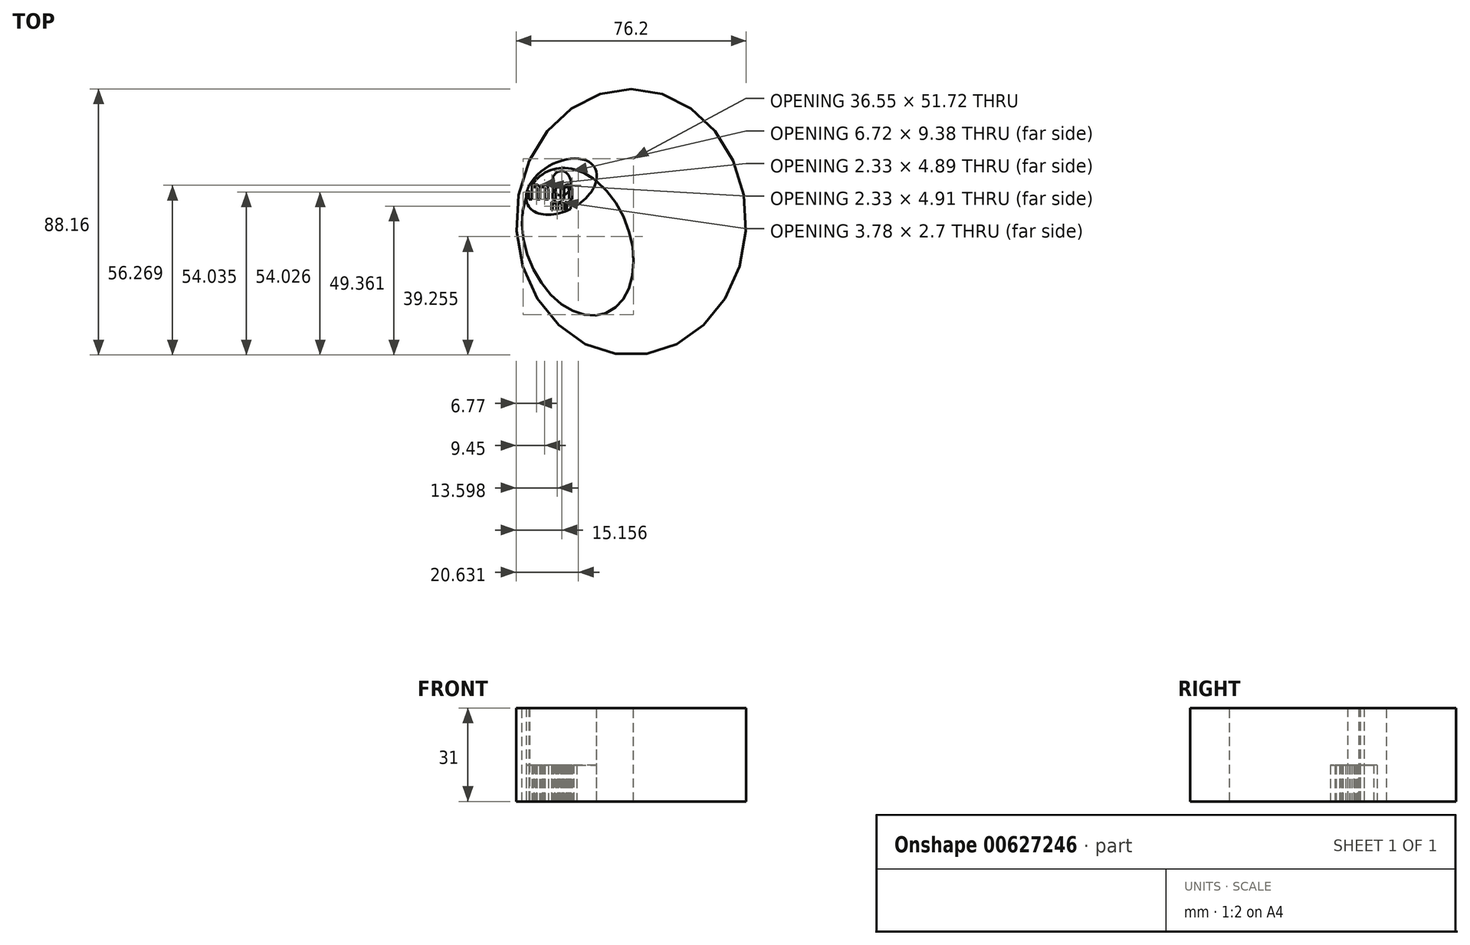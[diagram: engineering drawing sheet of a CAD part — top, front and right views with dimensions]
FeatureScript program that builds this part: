
annotation { "Feature Type Name" : "Feature", "Feature Type Description" : "" }
export const myFeature = defineFeature(function(context is Context, id is Id, definition is map)
    precondition{}
    {
        {
            var Q0;
            Q0=qCreatedBy(makeId("Top.planeOp"),FACE);
            var sketch = newSketch(context, id + "F0", { "sketchPlane" : qUnion([Q0])});
            skText(sketch, "E0", { "text": "mm", "fontName": "AllertaStencil-Regular.ttf"});
            skText(sketch, "E1", { "text": "mm", "fontName": "OpenSans-Regular.ttf"});
            skEllipse(sketch, "E2", {"center": v(-6.82, 3.93) * mm, "majorRadius": 6.35 * mm, "minorRadius": 2.55 * mm, "majorAxis": v(1, 0)});
            skEllipse(sketch, "E3", {"center": v(-5.46, 12.84) * mm, "majorRadius": 4.06 * mm, "minorRadius": 3.18 * mm, "majorAxis": v(0, -1)});
            skEllipse(sketch, "E4", {"center": v(-5.43, 11.73) * mm, "majorRadius": 7.98 * mm, "minorRadius": 12.7 * mm, "majorAxis": v(-0.49, 0.87)});
            skEllipse(sketch, "E5", {"center": v(17.67, 0) * mm, "majorRadius": 38.1 * mm, "minorRadius": 44.08 * mm, "majorAxis": v(1, 0)});
            skEllipse(sketch, "E6", {"center": v(0, -6.53) * mm, "majorRadius": 25.4 * mm, "minorRadius": 17.2 * mm, "majorAxis": v(-0.36, 0.93)});
            const initialGuessF0  = {"E0": [-0.01697, 0.0075, 1, 0, 0.00635], "E1": [-0.00915, 0.00393, 1, 0, 0.00357]};
            skSetInitialGuess(sketch, initialGuessF0);
            skSolve(sketch);
        }
        {
            var Q0;
            {var subQ16=sQuery(id+"F0.wireOp",EDGE,"E0.sketch_text.stroke-1");Q0=makeQuery(id+"F0.imprint","IMPRINT",FACE,{"disambiguationData":[TD([[makeQuery(id+"F0.imprint","IMPRINT",EDGE,{"derivedFrom":subQ16}),1.0]])]});}
            extrude(context, id + "F1", {"entities" : qUnion([Q0]), "depth" : 12 * mm, "offsetDistance" : 25.4 * mm});
        }
        {
            var Q0;
            Q0=makeQuery(id+"F0.imprint","IMPRINT",FACE,{"disambiguationData":[TD([[makeQuery(id+"F0.imprint","IMPRINT",EDGE,{"derivedFrom":sQuery(id+"F0.wireOp",EDGE,"E1.sketch_text.stroke-0")}),1.0]])]});
            extrude(context, id + "F2", {"entities" : qUnion([Q0]), "operationType" : NewBodyOperationType.ADD, "depth" : 12 * mm, "offsetDistance" : 25.4 * mm});
        }
        {
            var Q0;
            {var subQ2=sQuery(id+"F0.wireOp",EDGE,"E0.sketch_text.stroke-39");Q0=makeQuery(id+"F0.imprint","IMPRINT",FACE,{"disambiguationData":[TD([[makeQuery(id+"F0.imprint","IMPRINT",EDGE,{"derivedFrom":subQ2}),-1.0]])]});}
            var Q1;
            Q1=makeQuery(id+"F0.imprint","IMPRINT",FACE,{"disambiguationData":[TD([[makeQuery(id+"F0.imprint","IMPRINT",EDGE,{"derivedFrom":sQuery(id+"F0.wireOp",EDGE,"E0.sketch_text.stroke-60")}),-1.0]])]});
            var Q2;
            {var subQ0=sQuery(id+"F0.wireOp",EDGE,"E0.sketch_text.stroke-44");Q2=makeQuery(id+"F0.imprint","IMPRINT",FACE,{"disambiguationData":[TD([[makeQuery(id+"F0.imprint","IMPRINT",EDGE,{"derivedFrom":subQ0}),-1.0]])]});}
            var Q3;
            Q3 = qBodyType(qCreatedBy(id + "F0" ,EDGE), BodyType.WIRE);
            extrude(context, id + "F3", {"entities" : qUnion([Q0, Q1, Q2]), "operationType" : NewBodyOperationType.ADD, "surfaceOperationType" : NewSurfaceOperationType.ADD, "surfaceEntities" : qUnion([Q3]), "depth" : 12 * mm, "offsetDistance" : 25 * mm});
        }
        {
            var Q0;
            Q0=makeQuery(id+"F0.imprint","IMPRINT",FACE,{"disambiguationData":[TD([[makeQuery(id+"F0.imprint","IMPRINT",EDGE,{"derivedFrom":sQuery(id+"F0.wireOp",EDGE,"E5")}),1.0]])]});
            var Q1;
            Q1=sQuery(id+"F0.wireOp",EDGE,"E5");
            extrude(context, id + "F4", {"entities" : qUnion([Q0]), "operationType" : NewBodyOperationType.ADD, "surfaceOperationType" : NewSurfaceOperationType.ADD, "surfaceEntities" : qUnion([Q1]), "depth" : 6 * mm, "offsetDistance" : 25 * mm});
        }
        {
            var Q0;
            {var subQ0=sQuery(id+"F0.wireOp",EDGE,"E6");var subQ1=sQuery(id+"F0.wireOp",EDGE,"E4");Q0=makeQuery(id+"F4.boolean.opBoolean","MERGE",FACE,{"derivedFrom":[makeQuery(id+"FpXsGUjmTus6fVf_0.opExtrude","CAP_FACE",FACE,{"disambiguationData":[OSD([sQuery(id+"F0.wireOp",EDGE,"E1.sketch_text.stroke-28"),sQuery(id+"F0.wireOp",EDGE,"E1.sketch_text.stroke-33"),sQuery(id+"F0.wireOp",EDGE,"E1.sketch_text.stroke-34"),sQuery(id+"F0.wireOp",EDGE,"E1.sketch_text.stroke-35"),sQuery(id+"F0.wireOp",EDGE,"E1.sketch_text.stroke-54"),sQuery(id+"F0.wireOp",EDGE,"E1.sketch_text.stroke-55"),sQuery(id+"F0.wireOp",EDGE,"E2"),subQ1,subQ0])],"isStart":false}),makeQuery(id+"F4.opExtrude","CAP_FACE",FACE,{"disambiguationData":[OSD([sQuery(id+"F0.wireOp",EDGE,"E0.sketch_text.stroke-3"),sQuery(id+"F0.wireOp",EDGE,"E0.sketch_text.stroke-4"),subQ1,sQuery(id+"F0.wireOp",EDGE,"E5"),subQ0])],"isStart":false})]});}
            extrude(context, id + "F5", {"entities" : qUnion([Q0]), "operationType" : NewBodyOperationType.ADD, "depth" : 25 * mm, "offsetDistance" : 25 * mm});
        }
        {
            var Q0;
            Q0=sQuery(id+"F0.wireOp",EDGE,"E5");
            extrude(context, id + "F6", {"bodyType" : ToolBodyType.SURFACE, "surfaceEntities" : qUnion([Q0]), "depth" : 10 * mm, "offsetDistance" : 25 * mm});
        }
    });
